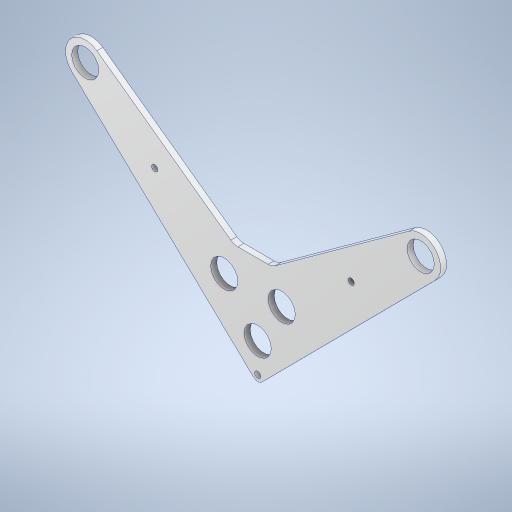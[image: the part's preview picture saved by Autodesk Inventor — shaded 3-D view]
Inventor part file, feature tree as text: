
AUTODESK INVENTOR PART (.ipt)
format: ipt  version: 2024.3 (Build 283343000, 343)  size: 278,016 bytes
history: native  units: in
note: dims shown in document units (in); Inventor stores cm internally (conversion verified against a paired STEP export)
features: extrude x1, sketch x1
ambient origin geometry x8: Origin, YZ Plane, XZ Plane, XY Plane, X Axis, Y Axis, Z Axis, Center Point
bodies: Body1 (feature_tree)
feature tree (2):
  extrude  "Extrusion2"  Depth=0.5in
  sketch  "Sketch1"  dims[d0=1.6in d1=2.4in d2=2.5in d3=1.7in d4=0.125in d5=1.13in d6=7.48in d7=4.0in d8=10.0in d9=1.13in d10=0.5in d11=0.125in d12=0.5in d13=0.5in d14=0.257in d15=0.257in d16=1.654in d19=0.25in d20=0.0in d21=0.5in d22=0.5in]
